# Revit family: Ceiling-Assembly_Component-Armstrong-MetalWorks_Clip-On-Panel-Full
name_source: partatom
category: Specialty Equipment
revit_build: Autodesk Revit Architecture 2012 (Build: 20110916_2132(x64)
units: mm (PartAtom-declared; Revit-internal decimal feet)

## types (1)
- Ceiling-Assembly_Component-Armstrong-MetalWorks_Clip-On-Panel-Full
    04 CSI = 09 22 00
    95 CSI = 09100
    Armstrong Category = Panels
    Assembly Code = C3030200
    Color Availability = Whitelume, Silverlume, Gun Metal, Satin Anodized, Lacquer Mill, Brushalume
    Description = 2' x 2' Panel - Butt Joint, Whitelume
    Item Number = 7110
    Length = 2' - 0"
    Manufacturer = Armstrong World Industries, Inc.
    Manufacturer Fax = 1 800-572-TECH
    Material = Metal
    Model = BP7110
    Panel = <By Category>
    Perforation Pattern = M1 - Unperforated, M14, M15, M16, M17, M18, M19
    Product Line = MetalWorks Clip-On
    Reveal = 0' - 0 1/4"
    Subcategory = Ceiling Panel/Tile/Plank
    Surface Finish = Factory-applied polyester paint
    Texture = Smooth
    URL = http://www.armstrong.com
    Weight Per Piece = 3.00 lb
    Width = 2' - 0"

## geometry (parser evidence)
native form markers: Blend x10, Sweep x4
no freeform markers — native parametric forms only
